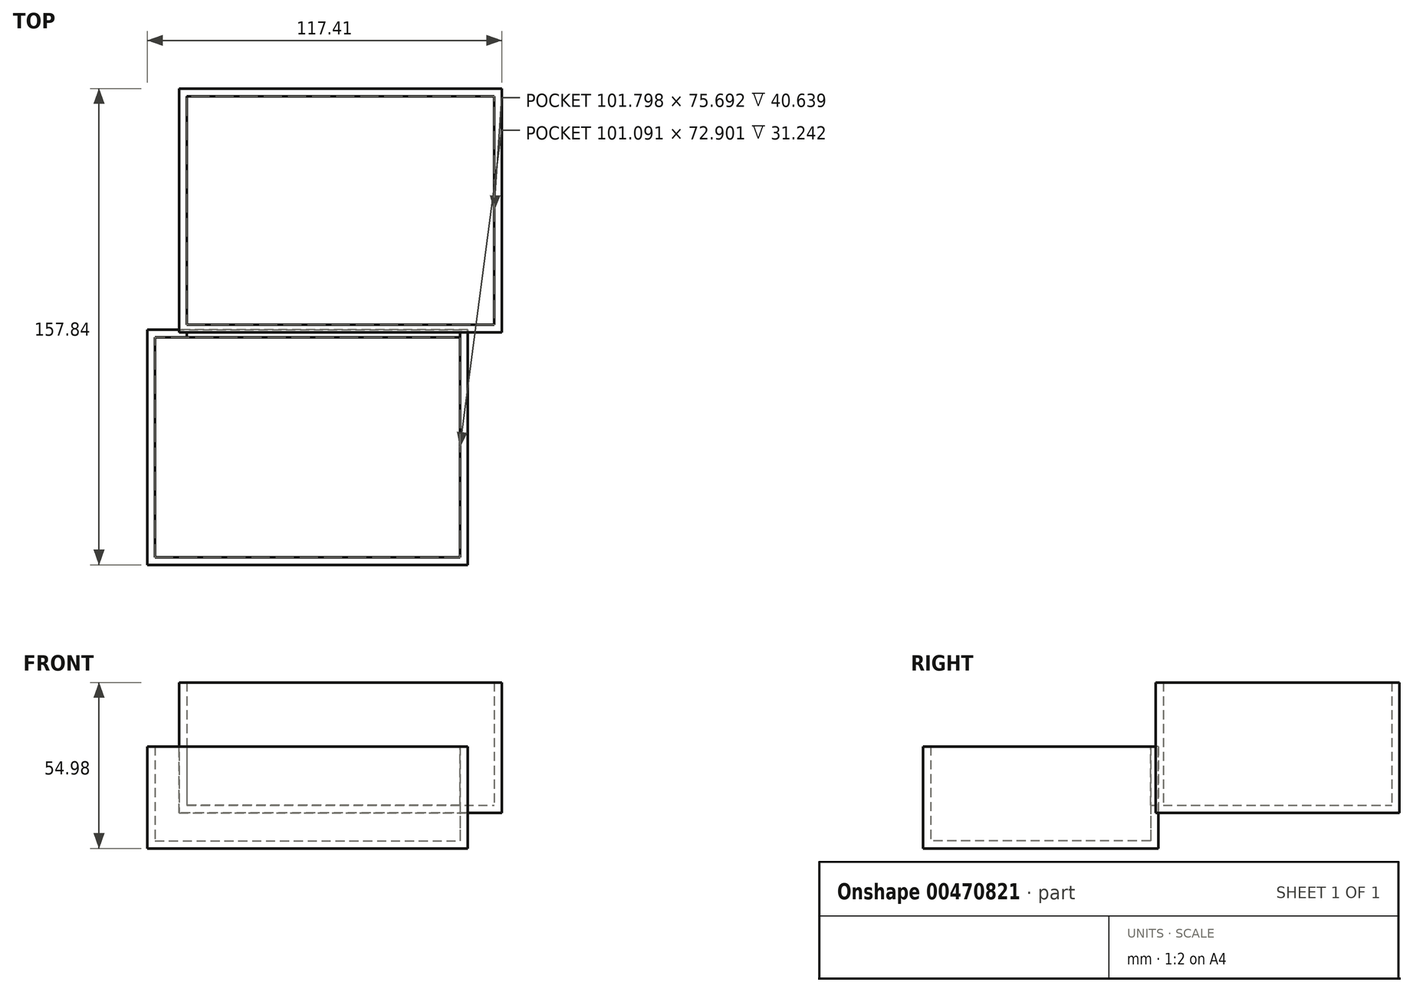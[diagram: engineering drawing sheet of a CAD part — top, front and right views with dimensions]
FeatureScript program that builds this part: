
annotation { "Feature Type Name" : "Feature", "Feature Type Description" : "" }
export const myFeature = defineFeature(function(context is Context, id is Id, definition is map)
    precondition{}
    {
        {
            var Q0;
            Q0=qCreatedBy(makeId("Front.planeOp"),FACE);
            var sketch = newSketch(context, id + "F0", { "sketchPlane" : qUnion([Q0])});
            skLineSegment(sketch, "E0.bottom", {"start": v(-57.87, 54.98) * mm, "end": v(49, 54.98) * mm});
            skLineSegment(sketch, "E0.top", {"start": v(-57.87, 11.8) * mm, "end": v(49, 11.8) * mm});
            skLineSegment(sketch, "E0.left", {"start": v(-57.87, 54.98) * mm, "end": v(-57.87, 11.8) * mm});
            skLineSegment(sketch, "E0.right", {"start": v(49, 54.98) * mm, "end": v(49, 11.8) * mm});
            skSolve(sketch);
        }
        {
            var Q0;
            Q0 = qSketchRegion(id + "F0", true);
            extrude(context, id + "F1", {"entities" : qUnion([Q0]), "depth" : 80.77 * mm});
        }
        {
            var Q0;
            Q0=makeQuery(id+"F1.opExtrude","SWEPT_FACE",FACE,{"disambiguationData":[OSD([sQuery(id+"F0.wireOp",EDGE,"E0.bottom")])]});
            shell(context, id + "F2", {"entities" : qUnion([Q0]), "thickness" : 2.54 * mm});
        }
        {
            var Q0;
            Q0=qCreatedBy(makeId("Top.planeOp"),FACE);
            var sketch = newSketch(context, id + "F3", { "sketchPlane" : qUnion([Q0])});
            skLineSegment(sketch, "E1.bottom", {"start": v(-68.4, -79.86) * mm, "end": v(37.77, -79.86) * mm});
            skLineSegment(sketch, "E1.top", {"start": v(-68.4, -157.84) * mm, "end": v(37.77, -157.84) * mm});
            skLineSegment(sketch, "E1.left", {"start": v(37.77, -79.86) * mm, "end": v(37.77, -157.84) * mm});
            skLineSegment(sketch, "E1.right", {"start": v(-68.4, -79.86) * mm, "end": v(-68.4, -157.84) * mm});
            skSolve(sketch);
        }
        {
            var Q0;
            Q0=makeQuery(id+"F3.imprint","IMPRINT",FACE,{"disambiguationData":[TD([[makeQuery(id+"F3.imprint","IMPRINT",EDGE,{"derivedFrom":sQuery(id+"F3.wireOp",EDGE,"E1.bottom")}),-1.0]])]});
            extrude(context, id + "F4", {"entities" : qUnion([Q0]), "operationType" : NewBodyOperationType.ADD, "depth" : 33.78 * mm});
        }
        {
            var Q0;
            Q0=makeQuery(id+"F4.opExtrude","CAP_FACE",FACE,{"disambiguationData":[OSD([sQuery(id+"F3.wireOp",EDGE,"E1.bottom"),sQuery(id+"F3.wireOp",EDGE,"E1.top"),sQuery(id+"F3.wireOp",EDGE,"E1.left"),sQuery(id+"F3.wireOp",EDGE,"E1.right")])],"isStart":false});
            shell(context, id + "F5", {"entities" : qUnion([Q0]), "thickness" : 2.54 * mm});
        }
    });
